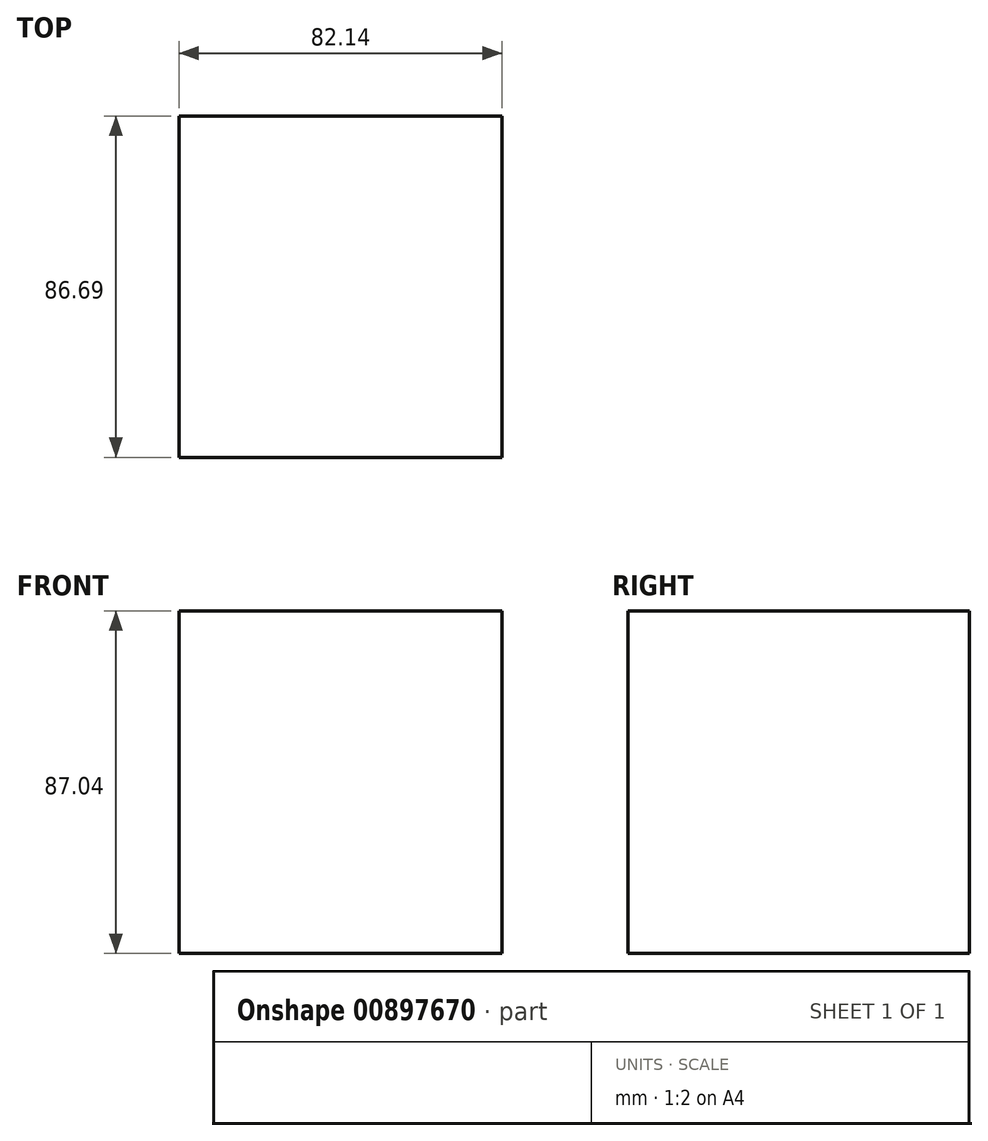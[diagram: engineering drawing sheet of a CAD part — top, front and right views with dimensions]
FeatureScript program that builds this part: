
annotation { "Feature Type Name" : "Feature", "Feature Type Description" : "" }
export const myFeature = defineFeature(function(context is Context, id is Id, definition is map)
    precondition{}
    {
        {
            var Q0;
            Q0=qCreatedBy(makeId("Front.planeOp"),FACE);
            var sketch = newSketch(context, id + "F0", { "sketchPlane" : qUnion([Q0])});
            skLineSegment(sketch, "E0", {"start": v(-40.78, 33.3) * mm, "end": v(-40.78, -53.75) * mm});
            skLineSegment(sketch, "E1", {"start": v(-40.78, 33.3) * mm, "end": v(41.36, 33.3) * mm});
            skLineSegment(sketch, "E2", {"start": v(-40.78, -53.75) * mm, "end": v(41.36, -53.75) * mm});
            skLineSegment(sketch, "E3", {"start": v(41.36, -53.75) * mm, "end": v(41.36, 33.3) * mm});
            skSolve(sketch);
        }
        {
            var Q0;
            Q0=makeQuery(id+"F0.imprint","IMPRINT",FACE,{"disambiguationData":[TD([[makeQuery(id+"F0.imprint","IMPRINT",EDGE,{"derivedFrom":sQuery(id+"F0.wireOp",EDGE,"E0")}),1.0]])]});
            extrude(context, id + "F1", {"entities" : qUnion([Q0]), "depth" : 86.7 * mm, "offsetDistance" : 25.4 * mm});
        }
    });
